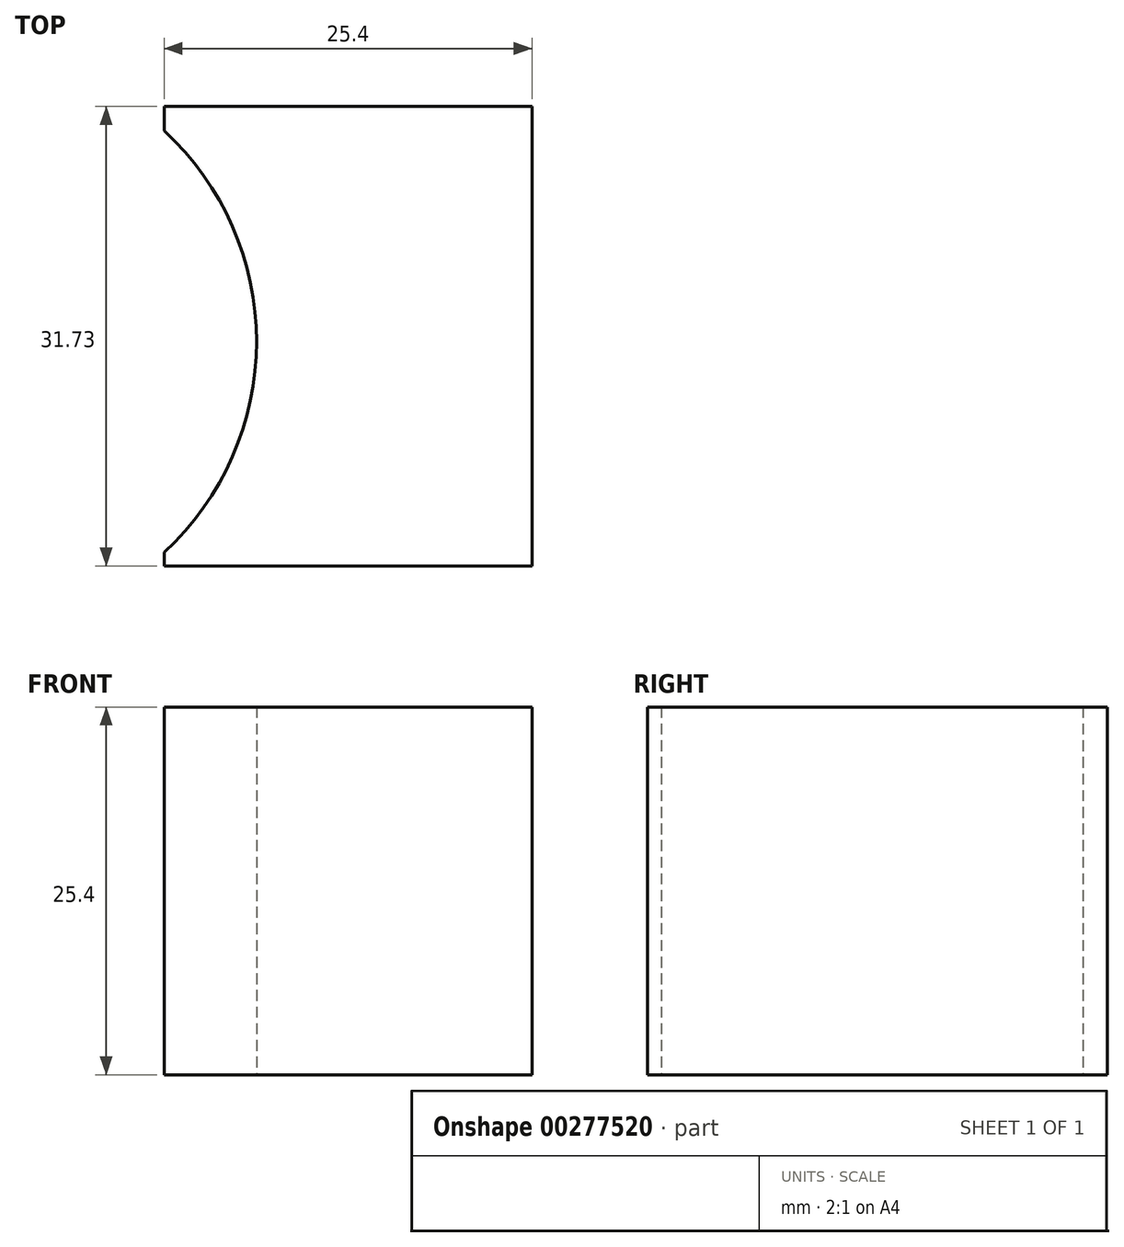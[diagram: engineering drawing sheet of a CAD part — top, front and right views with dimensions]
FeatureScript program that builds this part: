
annotation { "Feature Type Name" : "Feature", "Feature Type Description" : "" }
export const myFeature = defineFeature(function(context is Context, id is Id, definition is map)
    precondition{}
    {
        {
            var Q0;
            Q0=qCreatedBy(makeId("Top.planeOp"),FACE);
            var sketch = newSketch(context, id + "F0", { "sketchPlane" : qUnion([Q0])});
            skCircle(sketch, "E0", {"center": v(0, 0) * mm, "radius": 21.08 * mm});
            skPoint(sketch, "E1.startSnap0", {"position": v(38.83, -1.26) * mm});
            skLineSegment(sketch, "E2.bottom", {"start": v(13.43, 16.24) * mm, "end": v(38.83, 16.24) * mm});
            skLineSegment(sketch, "E2.top", {"start": v(13.43, -15.5) * mm, "end": v(38.83, -15.5) * mm});
            skLineSegment(sketch, "E2.left", {"start": v(13.43, 16.24) * mm, "end": v(13.43, -15.5) * mm});
            skLineSegment(sketch, "E2.right", {"start": v(38.83, 16.24) * mm, "end": v(38.83, -15.5) * mm});
            skCircle(sketch, "E3", {"center": v(0, 0) * mm, "radius": 19.81 * mm});
            skSolve(sketch);
        }
        {
            var Q0;
            {var subQ0=sQuery(id+"F0.wireOp",EDGE,"E2.left");Q0=makeQuery(id+"F0.imprint","IMPRINT",FACE,{"disambiguationData":[TD([[makeQuery(id+"F0.imprint","IMPRINT",EDGE,{"derivedFrom":subQ0}),-1.0]])]});}
            var Q1;
            {var subQ2=sQuery(id+"F0.wireOp",EDGE,"E2.bottom");Q1=makeQuery(id+"F0.imprint","IMPRINT",FACE,{"disambiguationData":[TD([[makeQuery(id+"F0.imprint","IMPRINT",EDGE,{"derivedFrom":subQ2}),-1.0]])]});}
            var Q2;
            {var subQ0=sQuery(id+"F0.wireOp",EDGE,"E2.left");Q2=makeQuery(id+"F0.imprint","IMPRINT",FACE,{"disambiguationData":[TD([[makeQuery(id+"F0.imprint","IMPRINT",EDGE,{"derivedFrom":subQ0}),1.0]])]});}
            extrude(context, id + "F1", {"entities" : qUnion([Q0, Q1, Q2]), "depth" : 25.4 * mm});
        }
        {
            var Q0;
            {var subQ0=sQuery(id+"F0.wireOp",EDGE,"E3");var subQ1=sQuery(id+"F0.wireOp",EDGE,"E2.left");var subQ2=makeQuery(id+"F0.imprint","INTERSECT",VERTEX,{"disambiguationData":[OD(0.0)],"derivedFrom":[subQ1,subQ0]});Q0=makeQuery(id+"F0.imprint","IMPRINT",FACE,{"disambiguationData":[TD([[makeQuery(id+"F0.imprint","IMPRINT",EDGE,{"disambiguationData":[TD([[subQ2,-1.0]])],"derivedFrom":subQ1}),-1.0]])]});}
            extrude(context, id + "F2", {"entities" : qUnion([Q0]), "operationType" : NewBodyOperationType.REMOVE, "depth" : 25.4 * mm});
        }
    });
